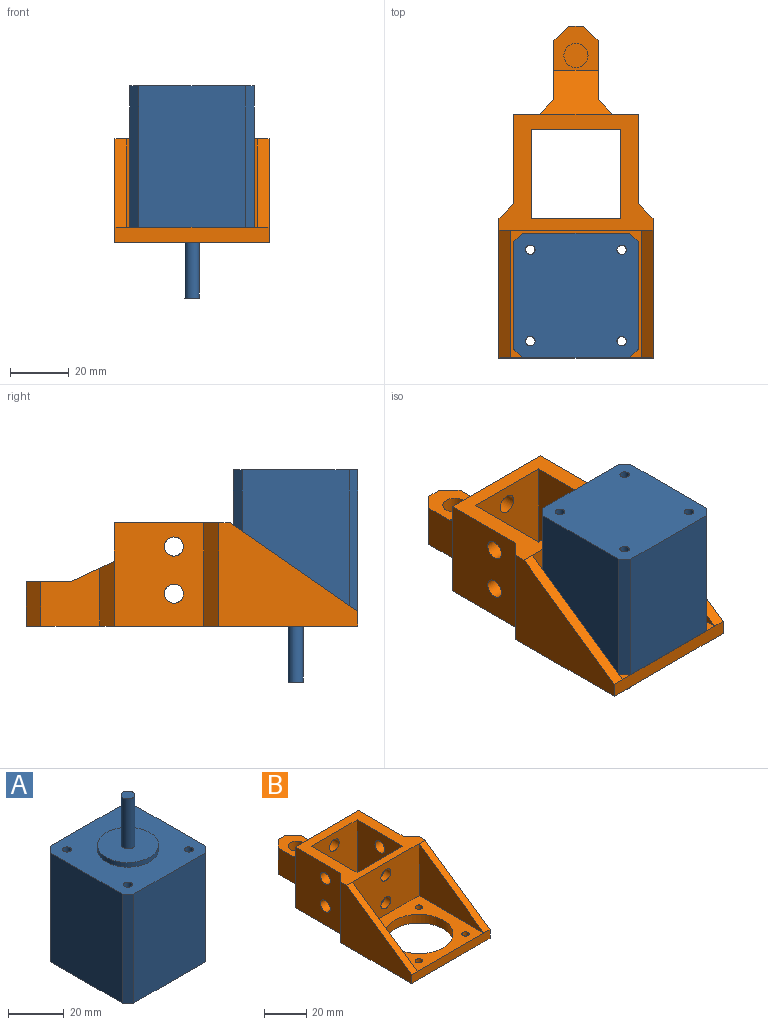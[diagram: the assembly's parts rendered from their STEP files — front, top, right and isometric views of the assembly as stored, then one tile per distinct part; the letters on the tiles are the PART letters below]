
ASSEMBLY  parts=2 mates=1
PART A: 18 faces, bbox 42.3x42.3x72 mm
  f0: plane 48x36.3mm, normal (-1,0,0), area 1742.4mm2, adj f8,f9,f12,f13
  f1: plane 48x36.3mm, normal (0,-1,0), area 1742.4mm2, adj f8,f9,f10,f12
  f2: plane 48x36.3mm, normal (1,0,0), area 1742.4mm2, adj f8,f9,f10,f11
  f3: cylinder r=1.6mm len=48mm, axis (0,0,-1), area 482.5mm2, adj f8,f9
  f4: cylinder r=1.6mm len=48mm, axis (0,0,-1), area 482.5mm2, adj f8,f9
  f5: cylinder r=1.6mm len=48mm, axis (0,0,-1), area 482.5mm2, adj f8,f9
  f6: cylinder r=1.6mm len=48mm, axis (0,0,-1), area 482.5mm2, adj f8,f9
  f7: plane 48x36.3mm, normal (0,1,0), area 1742.4mm2, adj f8,f9,f11,f13
  f8: plane 42.3x42.3mm, normal (0,0,1), area 1359mm2, adj f0,f1,f2,f3,f4,f5,f6,f7
  f9: plane 42.3x42.3mm, normal (0,0,-1), area 1739.1mm2, adj f0,f1,f2,f3,f4,f5,f6,f7
  f10: plane 48x3mm, normal (0.71,-0.71,0), area 203.6mm2, adj f1,f2,f8,f9
  f11: plane 48x3mm, normal (0.71,0.71,0), area 203.6mm2, adj f2,f7,f8,f9
  f12: plane 48x3mm, normal (-0.71,-0.71,0), area 203.6mm2, adj f0,f1,f8,f9
  f13: plane 48x3mm, normal (-0.71,0.71,0), area 203.6mm2, adj f0,f7,f8,f9
  f14: cylinder r=11mm len=22mm, axis (0,0,-1), area 138.2mm2, adj f8,f15
  f15: plane 22x22mm, normal (0,0,1), area 360.5mm2, adj f14,f16
  f16: cylinder r=2.5mm len=22mm, axis (0,0,-1), area 345.6mm2, adj f15,f17
  f17: plane 5x5mm, normal (0,0,1), area 19.6mm2, adj f16
PART B: 43 faces, bbox 52.3x112.7x35 mm
  f0: plane 43.3x30mm, normal (0,-0.57,0.82), area 210.7mm2, adj f6,f13,f36,f39
  f1: plane 43.3x30mm, normal (0,-0.57,0.82), area 210.7mm2, adj f6,f13,f37,f38
  f2: plane 44.3x43.3mm, normal (0,0,1), area 1075.5mm2, adj f6,f7,f8,f9,f10,f11,f38,f39
  f3: plane 35x30.37mm, normal (1,0,0), area 996.4mm2, adj f12,f13,f18,f19,f23,f42
  f4: plane 35x30.37mm, normal (-1,0,0), area 996.4mm2, adj f12,f13,f20,f21,f23,f41
  f5: plane 35x30.4mm, normal (0,1,0), area 997.6mm2, adj f12,f13,f14,f15,f16,f17
  f6: plane 52.3x5mm, normal (0,-1,0), area 261.5mm2, adj f0,f1,f2,f12,f36,f37
  f7: cylinder r=1.75mm len=5mm, axis (0,0,-1), area 55mm2, adj f2,f12
  f8: cylinder r=1.75mm len=5mm, axis (0,0,-1), area 55mm2, adj f2,f12
  f9: cylinder r=16mm len=32mm, axis (0,0,-1), area 502.7mm2, adj f2,f12
  f10: cylinder r=1.75mm len=5mm, axis (0,0,-1), area 55mm2, adj f2,f12
  f11: cylinder r=1.75mm len=5mm, axis (0,0,-1), area 55mm2, adj f2,f12
  f12: plane 112.67x52.3mm, normal (0,0,-1), area 2678.9mm2, adj f3,f4,f5,f6,f7,f8,f9,f10
  f13: plane 52.3x39.37mm, normal (0,0,1), area 807mm2, adj f0,f1,f3,f4,f5,f16,f17,f22
  f14: cylinder r=3.25mm len=6.5mm, axis (0,-1,0), area 81.7mm2, adj f5,f40
  f15: cylinder r=3.25mm len=6.5mm, axis (0,-1,0), area 81.7mm2, adj f5,f40
  f16: plane 35x30.37mm, normal (1,0,0), area 996.4mm2, adj f5,f12,f13,f20,f21,f22
  f17: plane 35x30.37mm, normal (-1,0,0), area 996.4mm2, adj f5,f12,f13,f18,f19,f22
  f18: cylinder r=3.25mm len=6.5mm, axis (-1,0,0), area 121.5mm2, adj f3,f17
  f19: cylinder r=3.25mm len=6.5mm, axis (-1,0,0), area 121.5mm2, adj f3,f17
  f20: cylinder r=3.25mm len=6.5mm, axis (-1,0,0), area 121.5mm2, adj f4,f16
  f21: cylinder r=3.25mm len=6.5mm, axis (-1,0,0), area 121.5mm2, adj f4,f16
  f22: plane 35x30.4mm, normal (0,-1,0), area 1030.8mm2, adj f12,f13,f16,f17,f30
  f23: plane 42.3x35mm, normal (0,1,0), area 897.3mm2, adj f3,f4,f12,f13,f30,f31,f32,f33
  f24: plane 20x19.67mm, normal (1,0,0), area 323.3mm2, adj f12,f28,f31,f32,f34
  f25: plane 20x19.67mm, normal (-1,0,0), area 323.3mm2, adj f12,f28,f31,f33,f35
  f26: cylinder r=4.1mm len=8.2mm, axis (0,0,-1), area 206.1mm2, adj f28,f29
  f27: plane 15x5mm, normal (0,1,0), area 75mm2, adj f12,f28,f34,f35
  f28: plane 15x15mm, normal (0,0,1), area 147.2mm2, adj f24,f25,f26,f27,f31,f34,f35
  f29: plane 8.2x8.2mm, normal (0,0,1), area 52.8mm2, adj f26
  f30: cylinder r=3.25mm len=6.5mm, axis (0,1,0), area 102.1mm2, adj f22,f23
  f31: plane 25x15mm, normal (0,0.42,0.91), area 275.9mm2, adj f23,f24,f25,f28,f32,f33
  f32: plane 22x5mm, normal (0.71,0.71,0), area 147.3mm2, adj f12,f23,f24,f31
  f33: plane 22x5mm, normal (-0.71,0.71,0), area 147.3mm2, adj f12,f23,f25,f31
  f34: plane 15x5mm, normal (0.71,0.71,0), area 106.1mm2, adj f12,f24,f27,f28
  f35: plane 15x5mm, normal (-0.71,0.71,0), area 106.1mm2, adj f12,f25,f27,f28
  f36: plane 47.3x35mm, normal (1,0,0), area 1006mm2, adj f0,f6,f12,f13,f42
  f37: plane 47.3x35mm, normal (-1,0,0), area 1006mm2, adj f1,f6,f12,f13,f41
  f38: plane 43.3x30mm, normal (1,0,0), area 649.5mm2, adj f1,f2,f40
  f39: plane 43.3x30mm, normal (-1,0,0), area 649.5mm2, adj f0,f2,f40
  f40: plane 44.3x30mm, normal (0,-1,0), area 1262.6mm2, adj f2,f13,f14,f15,f38,f39
  f41: plane 35x5mm, normal (-0.71,0.71,0), area 247.5mm2, adj f4,f12,f13,f37
  f42: plane 35x5mm, normal (0.71,0.71,0), area 247.5mm2, adj f3,f12,f13,f36
PLACE A rot(axis=(1,0,0),180deg) t=(-28.44,-25.67,74.41)mm
PLACE B t=(-28.44,-25.67,21.41)mm
MATE fastened A.f14 <-> B.f9  axis (0,0,-1) through (-28.44,-25.67,26.41)mm
